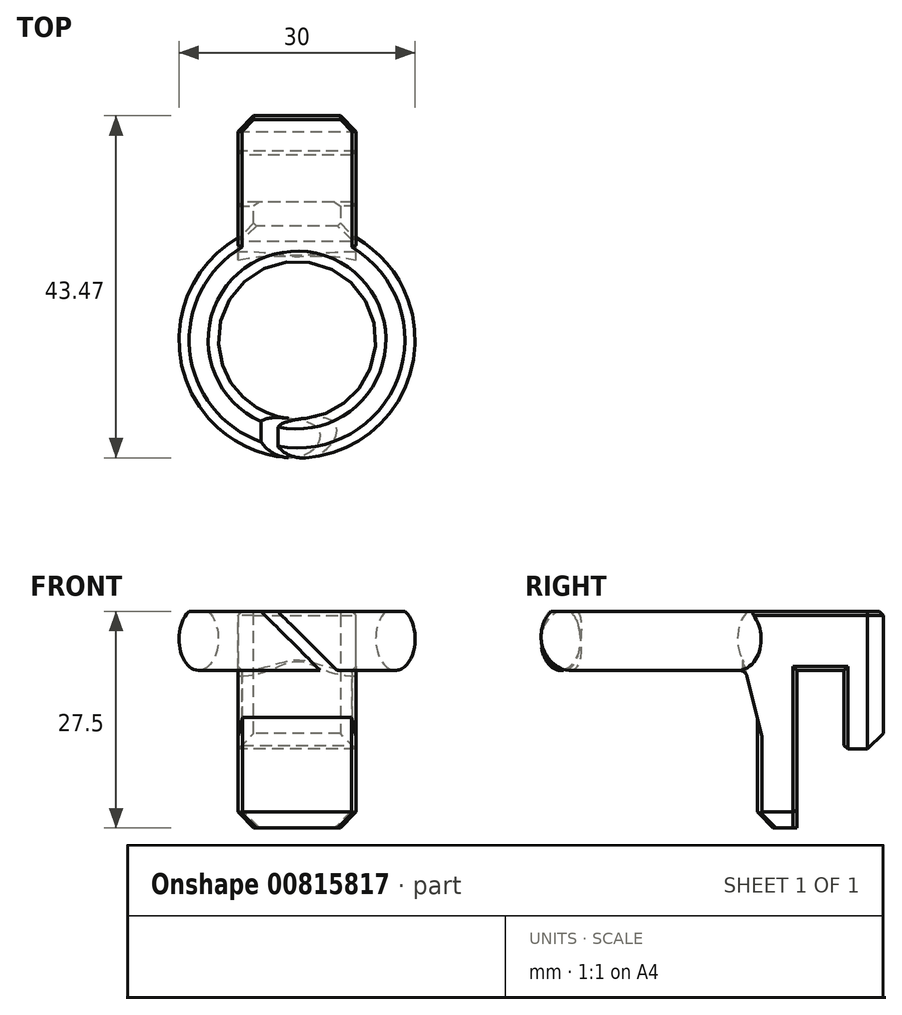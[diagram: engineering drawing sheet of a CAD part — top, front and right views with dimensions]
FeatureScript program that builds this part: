
annotation { "Feature Type Name" : "Feature", "Feature Type Description" : "" }
export const myFeature = defineFeature(function(context is Context, id is Id, definition is map)
    precondition{}
    {
        {
            var Q0;
            Q0=qCreatedBy(makeId("Front.planeOp"),FACE);
            var sketch = newSketch(context, id + "F0", { "sketchPlane" : qUnion([Q0])});
            skLineSegment(sketch, "E0", {"start": v(0, 10.58) * mm, "end": v(0, -9.7) * mm, "construction": true});
            skLineSegment(sketch, "E1", {"start": v(0, 0) * mm, "end": v(12.5, 0) * mm, "construction": true});
            skEllipse(sketch, "E2", {"center": v(12.5, 0) * mm, "majorRadius": 4 * mm, "minorRadius": 2.5 * mm, "majorAxis": v(0, 1)});
            skSolve(sketch);
        }
        {
            var Q0;
            Q0 = qSketchRegion(id + "F0", true);
            var Q1;
            Q1=sQuery(id+"F0.wireOp",EDGE,"E0");
            revolve(context, id + "F1", {"surfaceOperationType" : NewSurfaceOperationType.NEW, "entities" : qUnion([Q0]), "axis" : qUnion([Q1]), "revolveType" : RevolveType.FULL});
        }
        {
            var Q0;
            Q0=qCreatedBy(makeId("Right.planeOp"),FACE);
            var sketch = newSketch(context, id + "F2", { "sketchPlane" : qUnion([Q0])});
            skLineSegment(sketch, "E3", {"start": v(12.5, 5) * mm, "end": v(28.5, 5) * mm});
            skLineSegment(sketch, "E4", {"start": v(28.5, 5) * mm, "end": v(28.5, -14) * mm});
            skLineSegment(sketch, "E5", {"start": v(28.5, -14) * mm, "end": v(23.5, -14) * mm});
            skLineSegment(sketch, "E6", {"start": v(23.5, -14) * mm, "end": v(23.5, -4) * mm});
            skLineSegment(sketch, "E7", {"start": v(23.5, -4) * mm, "end": v(17.5, -4) * mm});
            skLineSegment(sketch, "E8", {"start": v(17.5, -4) * mm, "end": v(17.5, -24) * mm});
            skLineSegment(sketch, "E9", {"start": v(17.5, -24) * mm, "end": v(12.5, -24) * mm});
            skLineSegment(sketch, "E10", {"start": v(12.5, -24) * mm, "end": v(12.5, 5) * mm});
            skSolve(sketch);
        }
        {
            var Q0;
            Q0 = qSketchRegion(id + "F2", true);
            extrude(context, id + "F3", {"entities" : qUnion([Q0]), "operationType" : NewBodyOperationType.ADD, "endBound" : BoundingType.SYMMETRIC, "depth" : 15 * mm, "offsetDistance" : 25.4 * mm});
        }
        {
            var Q0;
            Q0=makeQuery(id+"F3.opExtrude","CAP_EDGE",EDGE,{"disambiguationData":[OSD([sQuery(id+"F2.wireOp",EDGE,"E3")])],"isStart":false});
            var Q1;
            Q1=makeQuery(id+"F3.opExtrude","CAP_EDGE",EDGE,{"disambiguationData":[OSD([sQuery(id+"F2.wireOp",EDGE,"E3")])],"isStart":true});
            var Q2;
            Q2=makeQuery(id+"F3.opExtrude","SWEPT_EDGE",EDGE,{"disambiguationData":[OSD([sQuery(id+"F2.wireOp",EDGE,"E3"),sQuery(id+"F2.wireOp",EDGE,"E4")])]});
            var Q3;
            Q3=makeQuery(id+"F3.opExtrude","CAP_EDGE",EDGE,{"disambiguationData":[OSD([sQuery(id+"F2.wireOp",EDGE,"E4")])],"isStart":true});
            var Q4;
            Q4=makeQuery(id+"F3.opExtrude","CAP_EDGE",EDGE,{"disambiguationData":[OSD([sQuery(id+"F2.wireOp",EDGE,"E4")])],"isStart":false});
            var Q5;
            Q5=makeQuery(id+"F3.opExtrude","SWEPT_EDGE",EDGE,{"disambiguationData":[OSD([sQuery(id+"F2.wireOp",EDGE,"E4"),sQuery(id+"F2.wireOp",EDGE,"E5")])]});
            var Q6;
            Q6=makeQuery(id+"F3.opExtrude","SWEPT_EDGE",EDGE,{"disambiguationData":[OSD([sQuery(id+"F2.wireOp",EDGE,"E9"),sQuery(id+"F2.wireOp",EDGE,"E10")])]});
            var Q7;
            Q7=makeQuery(id+"F3.opExtrude","CAP_EDGE",EDGE,{"disambiguationData":[OSD([sQuery(id+"F2.wireOp",EDGE,"E9")])],"isStart":false});
            var Q8;
            Q8=makeQuery(id+"F3.opExtrude","CAP_EDGE",EDGE,{"disambiguationData":[OSD([sQuery(id+"F2.wireOp",EDGE,"E9")])],"isStart":true});
            chamfer(context, id + "F4", {"entities" : qUnion([Q0, Q1, Q2, Q3, Q4, Q5, Q6, Q7, Q8]), "width" : 2 * mm, "tangentPropagation" : true});
        }
        {
            var Q0;
            Q0=makeQuery(id+"F3.opExtrude","CAP_EDGE",EDGE,{"disambiguationData":[OSD([sQuery(id+"F2.wireOp",EDGE,"E8")])],"isStart":true});
            var Q1;
            Q1=makeQuery(id+"F3.opExtrude","CAP_EDGE",EDGE,{"disambiguationData":[OSD([sQuery(id+"F2.wireOp",EDGE,"E8")])],"isStart":false});
            var Q2;
            Q2=makeQuery(id+"F3.opExtrude","CAP_EDGE",EDGE,{"disambiguationData":[OSD([sQuery(id+"F2.wireOp",EDGE,"E7")])],"isStart":false});
            var Q3;
            Q3=makeQuery(id+"F3.opExtrude","CAP_EDGE",EDGE,{"disambiguationData":[OSD([sQuery(id+"F2.wireOp",EDGE,"E7")])],"isStart":true});
            var Q4;
            Q4=makeQuery(id+"F3.opExtrude","CAP_EDGE",EDGE,{"disambiguationData":[OSD([sQuery(id+"F2.wireOp",EDGE,"E6")])],"isStart":true});
            var Q5;
            Q5=makeQuery(id+"F3.opExtrude","CAP_EDGE",EDGE,{"disambiguationData":[OSD([sQuery(id+"F2.wireOp",EDGE,"E6")])],"isStart":false});
            var Q6;
            Q6=makeQuery(id+"F3.opExtrude","SWEPT_EDGE",EDGE,{"disambiguationData":[OSD([sQuery(id+"F2.wireOp",EDGE,"E5"),sQuery(id+"F2.wireOp",EDGE,"E6")])]});
            var Q7;
            Q7=makeQuery(id+"F4.opChamfer","BLEND_EDGE",EDGE,{"blendedFrom":[makeQuery(id+"F3.opExtrude","CAP_EDGE",EDGE,{"disambiguationData":[OSD([sQuery(id+"F2.wireOp",EDGE,"E9")])],"isStart":false}),makeQuery(id+"F3.opExtrude","SWEPT_FACE",FACE,{"disambiguationData":[OSD([sQuery(id+"F2.wireOp",EDGE,"E8")])]})],"blendedInto":[makeQuery(id+"F3.opExtrude","SWEPT_FACE",FACE,{"disambiguationData":[OSD([sQuery(id+"F2.wireOp",EDGE,"E8")])]})]});
            var Q8;
            Q8=makeQuery(id+"F4.opChamfer","BLEND_EDGE",EDGE,{"blendedFrom":[makeQuery(id+"F3.opExtrude","CAP_EDGE",EDGE,{"disambiguationData":[OSD([sQuery(id+"F2.wireOp",EDGE,"E9")])],"isStart":true}),makeQuery(id+"F3.opExtrude","SWEPT_FACE",FACE,{"disambiguationData":[OSD([sQuery(id+"F2.wireOp",EDGE,"E8")])]})],"blendedInto":[makeQuery(id+"F3.opExtrude","SWEPT_FACE",FACE,{"disambiguationData":[OSD([sQuery(id+"F2.wireOp",EDGE,"E8")])]})]});
            chamfer(context, id + "F5", {"entities" : qUnion([Q0, Q1, Q2, Q3, Q4, Q5, Q6, Q7, Q8]), "width" : 0.5 * mm, "tangentPropagation" : true});
        }
        {
            var Q0;
            Q0=makeQuery(id+"F3.boolean.opBoolean","INTERSECT",EDGE,{"disambiguationData":[OD(0.0)],"derivedFrom":[makeQuery(id+"F1.opRevolve","SWEPT_FACE",FACE,{"disambiguationData":[OSD([sQuery(id+"F0.wireOp",EDGE,"E2")])]}),makeQuery(id+"F3.opExtrude","SWEPT_FACE",FACE,{"disambiguationData":[OSD([sQuery(id+"F2.wireOp",EDGE,"E10")])]})]});
            fillet(context, id + "F6", {"entities" : qUnion([Q0]), "radius" : 5 * mm, "tangentPropagation" : true, "allowEdgeOverflow" : false});
        }
        {
            var Q0;
            Q0=makeQuery(id+"F6.opFillet","BLEND_EDGE",EDGE,{"blendedFrom":[makeQuery(id+"F3.boolean.opBoolean","INTERSECT",EDGE,{"disambiguationData":[OD(0.0)],"derivedFrom":[makeQuery(id+"F1.opRevolve","SWEPT_FACE",FACE,{"disambiguationData":[OSD([sQuery(id+"F0.wireOp",EDGE,"E2")])]}),makeQuery(id+"F3.opExtrude","SWEPT_FACE",FACE,{"disambiguationData":[OSD([sQuery(id+"F2.wireOp",EDGE,"E10")])]})]}),makeQuery(id+"F3.opExtrude","SWEPT_FACE",FACE,{"disambiguationData":[OSD([sQuery(id+"F2.wireOp",EDGE,"E3")])]})],"blendedInto":[makeQuery(id+"F3.opExtrude","SWEPT_FACE",FACE,{"disambiguationData":[OSD([sQuery(id+"F2.wireOp",EDGE,"E3")])]})]});
            fillet(context, id + "F7", {"entities" : qUnion([Q0]), "radius" : 5 * mm, "tangentPropagation" : true, "allowEdgeOverflow" : false});
        }
        {
            var Q0;
            Q0=qCreatedBy(makeId("Right.planeOp"),FACE);
            var sketch = newSketch(context, id + "F8", { "sketchPlane" : qUnion([Q0])});
            skLineSegment(sketch, "E11", {"start": v(12.5, -10) * mm, "end": v(12.5, 0) * mm});
            skLineSegment(sketch, "E12", {"start": v(12.5, 0) * mm, "end": v(10, 0) * mm});
            skLineSegment(sketch, "E13", {"start": v(10, 0) * mm, "end": v(12.5, -10) * mm});
            skSolve(sketch);
        }
        {
            var Q0;
            Q0 = qSketchRegion(id + "F8", true);
            extrude(context, id + "F9", {"entities" : qUnion([Q0]), "operationType" : NewBodyOperationType.ADD, "endBound" : BoundingType.SYMMETRIC, "depth" : 15 * mm, "offsetDistance" : 25.4 * mm});
        }
        {
            var Q0;
            Q0=makeQuery(id+"F9.boolean.opBoolean","INTERSECT",EDGE,{"derivedFrom":[makeQuery(id+"F1.opRevolve","SWEPT_FACE",FACE,{"disambiguationData":[OSD([sQuery(id+"F0.wireOp",EDGE,"E2")])]}),makeQuery(id+"F9.opExtrude","SWEPT_FACE",FACE,{"disambiguationData":[OSD([sQuery(id+"F8.wireOp",EDGE,"E13")])]})]});
            var Q1;
            Q1=makeQuery(id+"F9.opExtrude","SWEPT_EDGE",EDGE,{"disambiguationData":[OSD([sQuery(id+"F8.wireOp",EDGE,"E11"),sQuery(id+"F8.wireOp",EDGE,"E13")])]});
            fillet(context, id + "F10", {"entities" : qUnion([Q0, Q1]), "radius" : 1 * mm, "tangentPropagation" : true, "allowEdgeOverflow" : false});
        }
        {
            var Q0;
            {var subQ0=sQuery(id+"F2.wireOp",EDGE,"E9");Q0=makeQuery(id+"F4.opChamfer","BLEND_EDGE",EDGE,{"blendedFrom":[makeQuery(id+"F3.opExtrude","SWEPT_EDGE",EDGE,{"disambiguationData":[OSD([subQ0,sQuery(id+"F2.wireOp",EDGE,"E10")])]}),makeQuery(id+"F3.opExtrude","CAP_EDGE",EDGE,{"disambiguationData":[OSD([subQ0])],"isStart":true})],"blendedInto":[]});}
            var Q1;
            {var subQ0=sQuery(id+"F2.wireOp",EDGE,"E9");Q1=makeQuery(id+"F4.opChamfer","BLEND_EDGE",EDGE,{"blendedFrom":[makeQuery(id+"F3.opExtrude","SWEPT_EDGE",EDGE,{"disambiguationData":[OSD([subQ0,sQuery(id+"F2.wireOp",EDGE,"E10")])]}),makeQuery(id+"F3.opExtrude","CAP_EDGE",EDGE,{"disambiguationData":[OSD([subQ0])],"isStart":false})],"blendedInto":[]});}
            chamfer(context, id + "F11", {"entities" : qUnion([Q0, Q1]), "width" : 0.5 * mm, "tangentPropagation" : true});
        }
        {
            var Q0;
            {var subQ0=sQuery(id+"F2.wireOp",EDGE,"E10");var subQ1=sQuery(id+"F2.wireOp",EDGE,"E9");Q0=makeQuery(id+"F3.boolean.opBoolean","SPLIT",EDGE,{"disambiguationData":[TD([makeQuery(id+"F3.opExtrude","SWEPT_FACE",FACE,{"disambiguationData":[OSD([subQ1])]})])],"derivedFrom":makeQuery(id+"F3.opExtrude","CAP_EDGE",EDGE,{"disambiguationData":[OSD([subQ0])],"isStart":true})});}
            var Q1;
            {var subQ0=sQuery(id+"F2.wireOp",EDGE,"E10");var subQ1=sQuery(id+"F2.wireOp",EDGE,"E9");Q1=makeQuery(id+"F3.boolean.opBoolean","SPLIT",EDGE,{"disambiguationData":[TD([makeQuery(id+"F3.opExtrude","SWEPT_FACE",FACE,{"disambiguationData":[OSD([subQ1])]})])],"derivedFrom":makeQuery(id+"F3.opExtrude","CAP_EDGE",EDGE,{"disambiguationData":[OSD([subQ0])],"isStart":false})});}
            chamfer(context, id + "F12", {"entities" : qUnion([Q0, Q1]), "width" : 0.6 * mm, "tangentPropagation" : true});
        }
        {
            var Q0;
            Q0=qCreatedBy(makeId("Front.planeOp"),FACE);
            var sketch = newSketch(context, id + "F13", { "sketchPlane" : qUnion([Q0])});
            skLineSegment(sketch, "E14", {"start": v(-1.06, 0) * mm, "end": v(-6.06, 5) * mm});
            skLineSegment(sketch, "E15", {"start": v(-6.06, 5) * mm, "end": v(-3.94, 5) * mm});
            skLineSegment(sketch, "E16", {"start": v(-3.94, 5) * mm, "end": v(6.06, -5) * mm});
            skLineSegment(sketch, "E17", {"start": v(6.06, -5) * mm, "end": v(3.94, -5) * mm});
            skLineSegment(sketch, "E18", {"start": v(3.94, -5) * mm, "end": v(-1.06, 0) * mm});
            skSolve(sketch);
        }
        {
            var Q0;
            Q0 = qSketchRegion(id + "F13", true);
            extrude(context, id + "F14", {"entities" : qUnion([Q0]), "operationType" : NewBodyOperationType.REMOVE, "depth" : 25 * mm, "offsetDistance" : 25 * mm});
        }
        {
            var Q0;
            Q0=qCreatedBy(makeId("Front.planeOp"),FACE);
            var sketch = newSketch(context, id + "F15", { "sketchPlane" : qUnion([Q0])});
            skLineSegment(sketch, "E19.bottom", {"start": v(-28.46, 11.77) * mm, "end": v(26.78, 11.77) * mm});
            skLineSegment(sketch, "E19.top", {"start": v(-28.46, 3.5) * mm, "end": v(26.78, 3.5) * mm});
            skLineSegment(sketch, "E19.left", {"start": v(-28.46, 11.77) * mm, "end": v(-28.46, 3.5) * mm});
            skLineSegment(sketch, "E19.right", {"start": v(26.78, 11.77) * mm, "end": v(26.78, 3.5) * mm});
            skSolve(sketch);
        }
        {
            var Q0;
            Q0=makeQuery(id+"F15.imprint","IMPRINT",FACE,{"disambiguationData":[TD([[makeQuery(id+"F15.imprint","IMPRINT",EDGE,{"derivedFrom":sQuery(id+"F15.wireOp",EDGE,"E19.bottom")}),-1.0]])]});
            extrude(context, id + "F16", {"entities" : qUnion([Q0]), "operationType" : NewBodyOperationType.REMOVE, "endBound" : BoundingType.SYMMETRIC, "oppositeDirection" : true, "depth" : 100 * mm, "offsetDistance" : 25 * mm});
        }
    });
